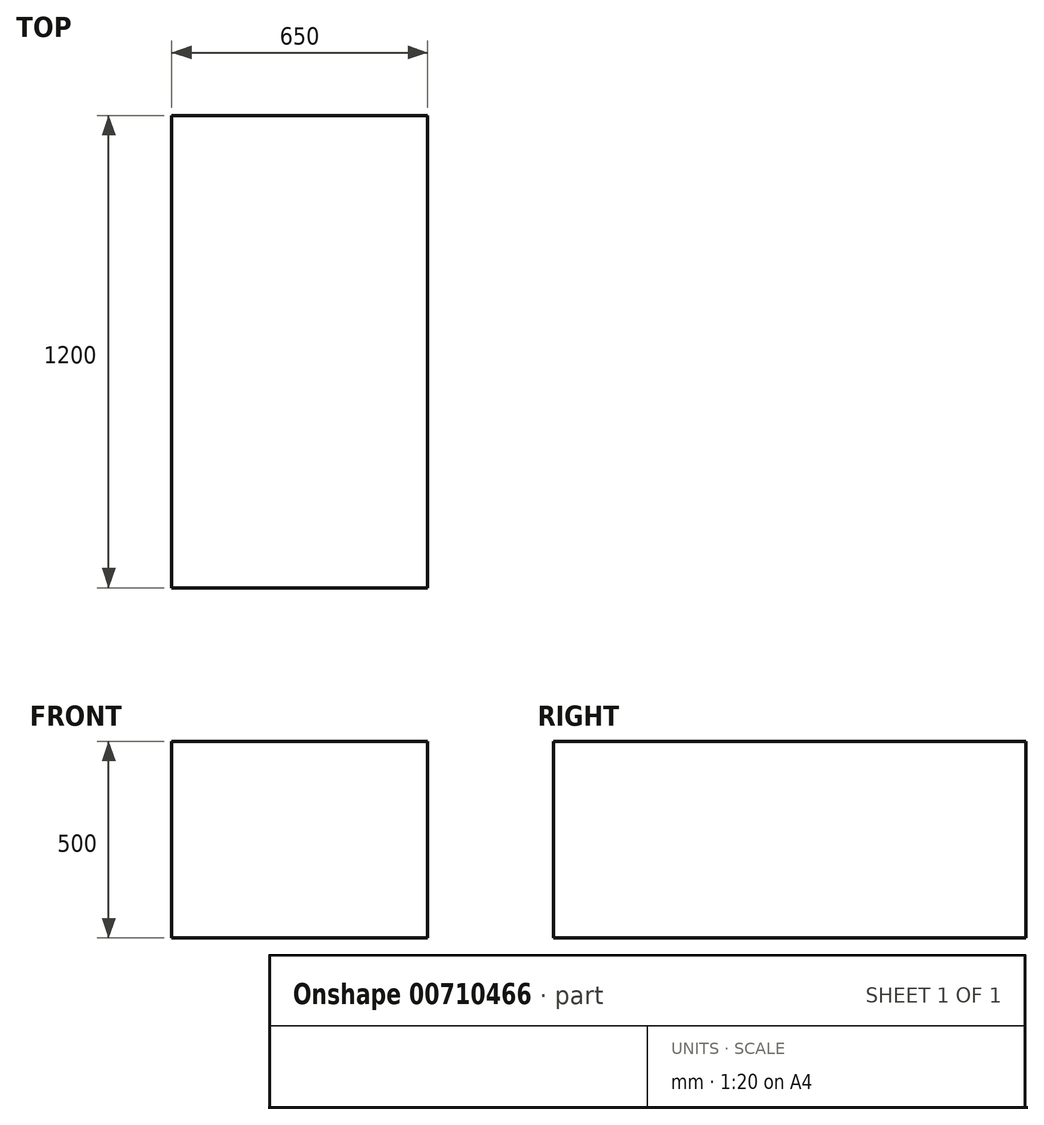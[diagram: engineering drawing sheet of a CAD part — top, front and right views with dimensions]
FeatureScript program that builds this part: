
annotation { "Feature Type Name" : "Feature", "Feature Type Description" : "" }
export const myFeature = defineFeature(function(context is Context, id is Id, definition is map)
    precondition{}
    {
        {
            var Q0;
            Q0=qCreatedBy(makeId("Top.planeOp"),FACE);
            var sketch = newSketch(context, id + "F0", { "sketchPlane" : qUnion([Q0])});
            skLineSegment(sketch, "E0.bottom", {"start": v(325, 600) * mm, "end": v(-325, 600) * mm});
            skLineSegment(sketch, "E0.top", {"start": v(325, -600) * mm, "end": v(-325, -600) * mm});
            skLineSegment(sketch, "E0.left", {"start": v(325, 600) * mm, "end": v(325, -600) * mm});
            skLineSegment(sketch, "E0.right", {"start": v(-325, 600) * mm, "end": v(-325, -600) * mm});
            skPoint(sketch, "E0.middle", {"position": v(0, 0) * mm});
            skSolve(sketch);
        }
        {
            var Q0;
            Q0=makeQuery(id+"F0.imprint","IMPRINT",FACE,{"disambiguationData":[TD([[makeQuery(id+"F0.imprint","IMPRINT",EDGE,{"derivedFrom":sQuery(id+"F0.wireOp",EDGE,"E0.bottom")}),1.0]])]});
            extrude(context, id + "F1", {"entities" : qUnion([Q0]), "depth" : 500 * mm, "offsetDistance" : 25 * mm});
        }
    });
